# Revit family: Electronics_Amplifiers_Biamp_Vocia_Networked_VA-4300CV___
name_source: partatom
category: Communication Devices
units: mm (PartAtom-declared; Revit-internal decimal feet)

## family parameters
Cut with Voids When Loaded = Yes
Host = Face
Maintain Annotation Orientation = No
OmniClass Number = 23.85.10.11.14.14.17
OmniClass Title = Sound Amplifiers
Part Type = Normal
Room Calculation Point = No
Round Connector Dimension = Use Diameter
Shared = No

## types (1)
- VA-4300CV
    Altitude = 0-10,000 ft (0-3000m) MSL
    Amplifier Topology = Class D
    Apparent Load = 432 VA
    Channels = 4 – fixed
    Compliance = EN 54-16 certified  FCC Part 15B (USA) CE Marked (Europe) RCM (Australia) RoHS Directive (Europe)
    Connector Description = 100-240VAC; 50/60Hz; 3.6-1.5A
    Current = 4 A
    Default Elevation = 48 "
    Depth = 17.5 "
    Description = Vocia® VA-4300CV Networked Amplifier
    Extended Audio Delay = Up to 32 Seconds (10km) per channel
    Failover Support = Chassis or Channel 1:1, 3:1
    Frequency Response = 20Hz-20kHz: +/- 1dB
    Height = 3.5 "
    Housing Material = Biamp - Metal - Silver
    Humidity = 0-95% relative humidity (non-condensing)
    Inputs = CobraNet 20 bits,  48kHz, 5-1/3ms (fixed)
    Inter-channel Isolation = 20Hz-20kHz at rated power: > 80dB
    Intermodulation distortion = SMPTE at continuous power: < 0.35% at 100V <0.65% at 70V
    Line monitoring = Passive end of line monitoring (PLD-2), Active end of line monitoring (ELD-1), Impedance monitoring, Pilot tone generation
    Manufacturer = Biamp
    Model = Vocia VA-4300CV
    Network Connection = Dual RJ-45 inputs for network redundancy
    Number of Poles = 1
    Power Factor = 1
    Power Note = Amplifier has battery back-up
    Product Documentation Link = https://downloads.biamp.com
    Product Page URL = https://www.biamp.com
    Product data url = https://www.bimobject.com
    Signal to Noise Ratio = 20Hz-20kHz, unweighted at rated power: > 100dB
    THD+N = 20Hz-20kHz, at rated power: < 0.3%
    Temperature Range = 18 - 108° F (-8°C - 42°C)
    Total Output Power = 4x300W
    URL = https://www.biamp.com
    Voltage = 120 V
    Watts per channel = 300W 70V/100V constant voltage
    Weight = 22.30 lbf
    Width = 19 "

## geometry (parser evidence)
native form markers: Sweep x2
no freeform markers — native parametric forms only
